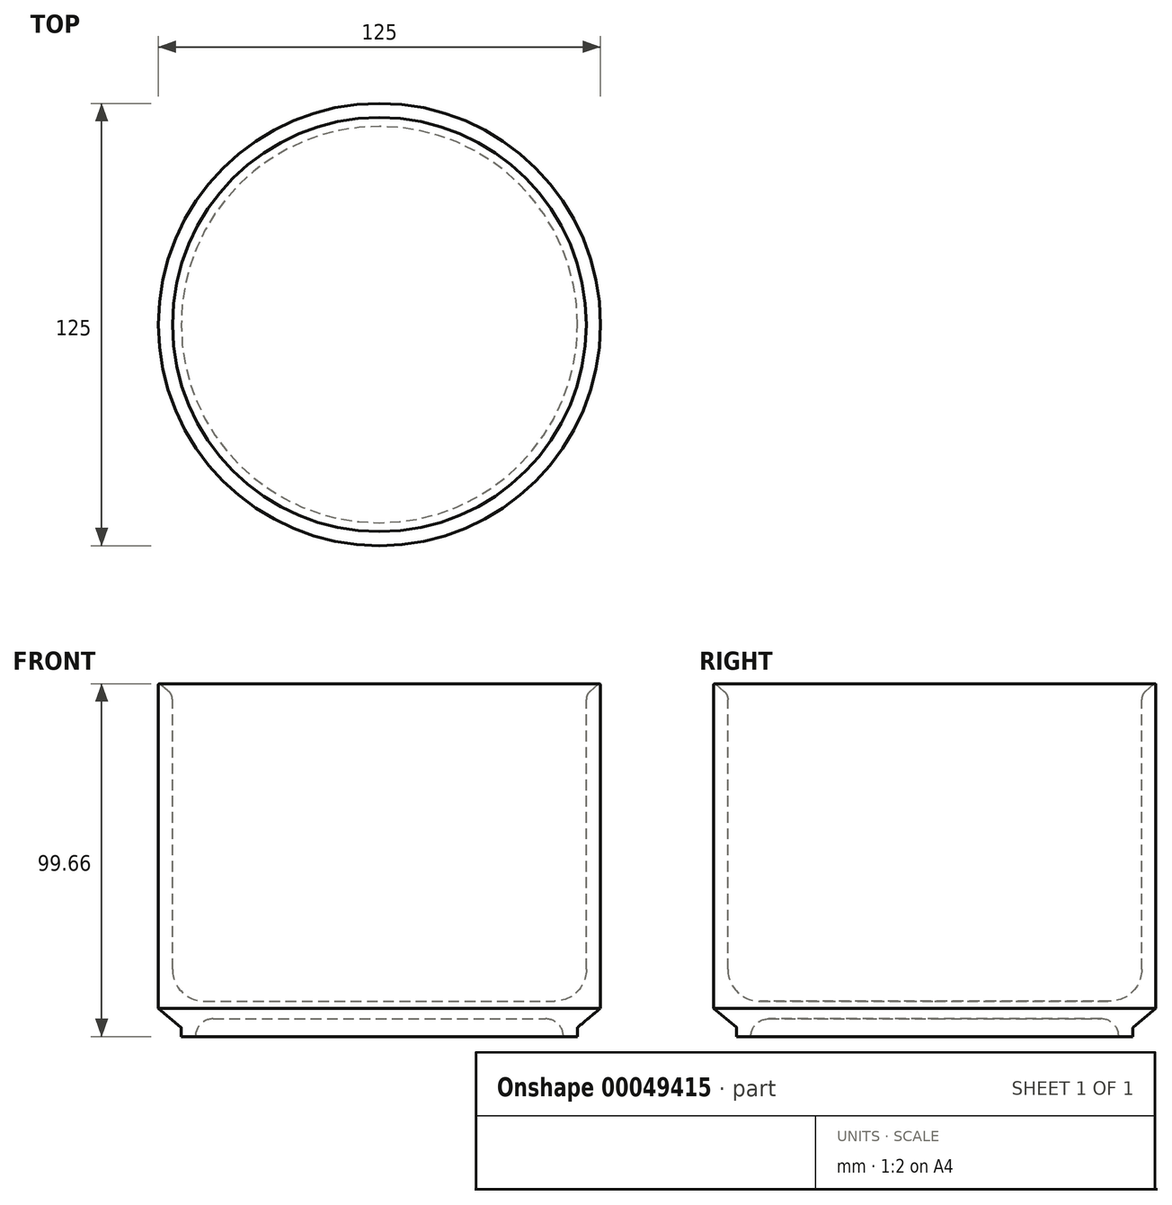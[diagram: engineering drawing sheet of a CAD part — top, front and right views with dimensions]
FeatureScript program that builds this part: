
annotation { "Feature Type Name" : "Feature", "Feature Type Description" : "" }
export const myFeature = defineFeature(function(context is Context, id is Id, definition is map)
    precondition{}
    {
        {
            var Q0;
            Q0=qCreatedBy(makeId("Top.planeOp"),FACE);
            var sketch = newSketch(context, id + "F0", { "sketchPlane" : qUnion([Q0])});
            skCircle(sketch, "E0", {"center": v(0, 0) * mm, "radius": 62.5 * mm});
            skSolve(sketch);
        }
        {
            var Q0;
            Q0=makeQuery(id+"F0.imprint","IMPRINT",FACE,{"disambiguationData":[TD([[makeQuery(id+"F0.imprint","IMPRINT",EDGE,{"derivedFrom":sQuery(id+"F0.wireOp",EDGE,"E0")}),1.0]])]});
            extrude(context, id + "F1", {"entities" : qUnion([Q0]), "depth" : 100 * mm});
        }
        {
            var Q0;
            Q0=qCreatedBy(makeId("Right.planeOp"),FACE);
            var sketch = newSketch(context, id + "F2", { "sketchPlane" : qUnion([Q0])});
            skLineSegment(sketch, "E1.bottom", {"start": v(56, 0) * mm, "end": v(62.5, 0) * mm});
            skLineSegment(sketch, "E1.right", {"start": v(62.5, 0) * mm, "end": v(62.5, 8) * mm});
            skLineSegment(sketch, "E2", {"start": v(0, 0) * mm, "end": v(0, 100) * mm, "construction": true});
            skLineSegment(sketch, "E3", {"start": v(56, 0) * mm, "end": v(56, 2.55) * mm});
            skLineSegment(sketch, "E4", {"start": v(56, 2.55) * mm, "end": v(62.5, 8) * mm});
            skSolve(sketch);
        }
        {
            var Q0;
            Q0 = qSketchRegion(id + "F2", true);
            var Q1;
            Q1=sQuery(id+"F2.wireOp",EDGE,"E2");
            revolve(context, id + "F3", {"operationType" : NewBodyOperationType.REMOVE, "entities" : qUnion([Q0]), "axis" : qUnion([Q1]), "revolveType" : RevolveType.FULL, "oppositeDirection" : true});
        }
        {
            var Q0;
            Q0=makeQuery(id+"F1.opExtrude","CAP_FACE",FACE,{"disambiguationData":[OSD([sQuery(id+"F0.wireOp",EDGE,"E0")])],"isStart":true});
            var sketch = newSketch(context, id + "F4", { "sketchPlane" : qUnion([Q0])});
            skCircle(sketch, "E5", {"center": v(0, 0) * mm, "radius": 52 * mm});
            skSolve(sketch);
        }
        {
            var Q0;
            Q0 = qSketchRegion(id + "F4", true);
            extrude(context, id + "F5", {"entities" : qUnion([Q0]), "operationType" : NewBodyOperationType.REMOVE, "oppositeDirection" : true, "depth" : 5 * mm});
        }
        {
            var Q0;
            Q0=makeQuery(id+"F5.boolean.opBoolean","COPY",EDGE,{"derivedFrom":makeQuery(id+"F5.opExtrude","CAP_EDGE",EDGE,{"disambiguationData":[OSD([sQuery(id+"F4.wireOp",EDGE,"E5")])],"isStart":false})});
            fillet(context, id + "F6", {"entities" : qUnion([Q0]), "radius" : 5 * mm, "tangentPropagation" : true, "allowEdgeOverflow" : false});
        }
        {
            var Q0;
            Q0=qCreatedBy(makeId("Front.planeOp"),FACE);
            var sketch = newSketch(context, id + "F7", { "sketchPlane" : qUnion([Q0])});
            skLineSegment(sketch, "E6", {"start": v(-62.5, 100) * mm, "end": v(-58.5, 96.64) * mm});
            skLineSegment(sketch, "E7", {"start": v(-58.5, 96.64) * mm, "end": v(-58.5, 10) * mm});
            skLineSegment(sketch, "E8", {"start": v(-58.5, 10) * mm, "end": v(0, 10) * mm});
            skLineSegment(sketch, "E9", {"start": v(0, 10) * mm, "end": v(0, 100) * mm});
            skLineSegment(sketch, "E10", {"start": v(-62.5, 100) * mm, "end": v(0, 100) * mm});
            skSolve(sketch);
        }
        {
            var Q0;
            Q0 = qSketchRegion(id + "F7", true);
            var Q1;
            Q1=sQuery(id+"F7.wireOp",EDGE,"E9");
            revolve(context, id + "F8", {"operationType" : NewBodyOperationType.REMOVE, "entities" : qUnion([Q0]), "axis" : qUnion([Q1]), "revolveType" : RevolveType.FULL, "oppositeDirection" : true});
        }
        {
            var Q0;
            Q0=makeQuery(id+"F3.boolean.opBoolean","COPY",EDGE,{"derivedFrom":makeQuery(id+"F3.opRevolve","SWEPT_EDGE",EDGE,{"disambiguationData":[OSD([sQuery(id+"F2.wireOp",EDGE,"E1.top"),sQuery(id+"F2.wireOp",EDGE,"E1.right")])]})});
            var Q1;
            Q1=makeQuery(id+"F8.boolean.opBoolean","COPY",EDGE,{"derivedFrom":makeQuery(id+"F8.opRevolve","SWEPT_EDGE",EDGE,{"disambiguationData":[OSD([sQuery(id+"F7.wireOp",EDGE,"E6"),sQuery(id+"F7.wireOp",EDGE,"E7")])]})});
            fillet(context, id + "F9", {"entities" : qUnion([Q0, Q1]), "radius" : 3 * mm, "tangentPropagation" : true, "allowEdgeOverflow" : false});
        }
        {
            var Q0;
            Q0=makeQuery(id+"F8.boolean.opBoolean","MERGE",EDGE,{"derivedFrom":[makeQuery(id+"F1.opExtrude","CAP_EDGE",EDGE,{"disambiguationData":[OSD([sQuery(id+"F0.wireOp",EDGE,"E0")])],"isStart":false}),makeQuery(id+"F8.opRevolve","SWEPT_EDGE",EDGE,{"disambiguationData":[OSD([sQuery(id+"F7.wireOp",EDGE,"E6"),sQuery(id+"F7.wireOp",EDGE,"E10")])]})]});
            var Q1;
            Q1=makeQuery(id+"F6.opFillet","BLEND_EDGE",EDGE,{"blendedFrom":[makeQuery(id+"F5.boolean.opBoolean","COPY",EDGE,{"derivedFrom":makeQuery(id+"F5.opExtrude","CAP_EDGE",EDGE,{"disambiguationData":[OSD([sQuery(id+"F4.wireOp",EDGE,"E5")])],"isStart":false})}),makeQuery(id+"F1.opExtrude","CAP_FACE",FACE,{"disambiguationData":[OSD([sQuery(id+"F0.wireOp",EDGE,"E0")])],"isStart":true})],"blendedInto":[makeQuery(id+"F1.opExtrude","CAP_FACE",FACE,{"disambiguationData":[OSD([sQuery(id+"F0.wireOp",EDGE,"E0")])],"isStart":true})]});
            var Q2;
            Q2=makeQuery(id+"F3.boolean.opBoolean","COPY",EDGE,{"derivedFrom":makeQuery(id+"F3.opRevolve","SWEPT_EDGE",EDGE,{"disambiguationData":[OSD([sQuery(id+"F2.wireOp",EDGE,"E1.bottom"),sQuery(id+"F2.wireOp",EDGE,"E3")])]})});
            var Q3;
            Q3=makeQuery(id+"F3.boolean.opBoolean","COPY",EDGE,{"derivedFrom":makeQuery(id+"F3.opRevolve","SWEPT_EDGE",EDGE,{"disambiguationData":[OSD([sQuery(id+"F2.wireOp",EDGE,"E3"),sQuery(id+"F2.wireOp",EDGE,"E4")])]})});
            fillet(context, id + "F10", {"entities" : qUnion([Q0, Q1, Q2, Q3]), "radius" : 0.3 * mm, "tangentPropagation" : true, "allowEdgeOverflow" : false});
        }
        {
            var Q0;
            Q0=makeQuery(id+"F8.boolean.opBoolean","COPY",EDGE,{"derivedFrom":makeQuery(id+"F8.opRevolve","SWEPT_EDGE",EDGE,{"disambiguationData":[OSD([sQuery(id+"F7.wireOp",EDGE,"E7"),sQuery(id+"F7.wireOp",EDGE,"E8")])]})});
            fillet(context, id + "F11", {"entities" : qUnion([Q0]), "radius" : 9 * mm, "tangentPropagation" : true, "allowEdgeOverflow" : false});
        }
    });
